# Revit family: revitupgrade
name_source: partatom
category: Furniture
units: mm (PartAtom-declared; Revit-internal decimal feet)

## family parameters
Always vertical = Yes
Cut with Voids When Loaded = No
Enable Cutting in Views = No
Render Appearance Source = Family Geometry
Room Calculation Point = No
Shared = No
Work Plane-Based = No

## types (11) — shared parameters
Arm Cap Finish = Steelcase_Paint_7207_Black
Assembly Code = E2020200
Caster Finish = Steelcase_Plastic_6205_Black
Default Elevation = 0.00"
Description = The Kármán Line is where the atmosphere meets space, weightlessness becomes possible and going beyond becomes reality. That spirit is captured in Steelcase Karman.
Manufacturer = Steelcase
Release Date = February 2022
Style Number(s) = 419A000
URL = https://www.steelcase.com

## per-type parameters (varying)
| type | Arms | Base No Arms | Caster | Caster No Arms | Fixed Arms | Glide | Glide No Arms | Height Adjustable Arms | Hubble | Not Glide |
| HWPD Arms_Glide | Yes | No | No | No | No | Yes | No | Yes | No | No |
| HWPD Arms_Caster | Yes | No | Yes | No | No | No | No | Yes | No | Yes |
| Height Adjustable Arms_Glide | Yes | No | No | No | No | Yes | No | Yes | No | No |
| Height Adjustable Arms_Caster | Yes | No | Yes | No | No | No | No | Yes | No | Yes |
| Height Adjustable Arms_Hubble | Yes | No | No | No | No | No | No | Yes | Yes | Yes |
| Fixed Arms_Glide | Yes | No | No | No | Yes | Yes | No | No | No | No |
| Fixed Arms_Caster | Yes | No | Yes | No | Yes | No | No | No | No | Yes |
| Fixed Arms_Hubble | Yes | No | No | No | Yes | No | No | No | Yes | Yes |
| Armless_Glide | No | Yes | No | No | No | Yes | Yes | No | No | No |
| Armless_Caster | No | Yes | No | Yes | No | No | No | No | No | No |
| Armless_Hubble | No | Yes | No | Yes | No | No | No | No | Yes | No |

## geometry (parser evidence)
native form markers: Sweep x2
no freeform markers — native parametric forms only
